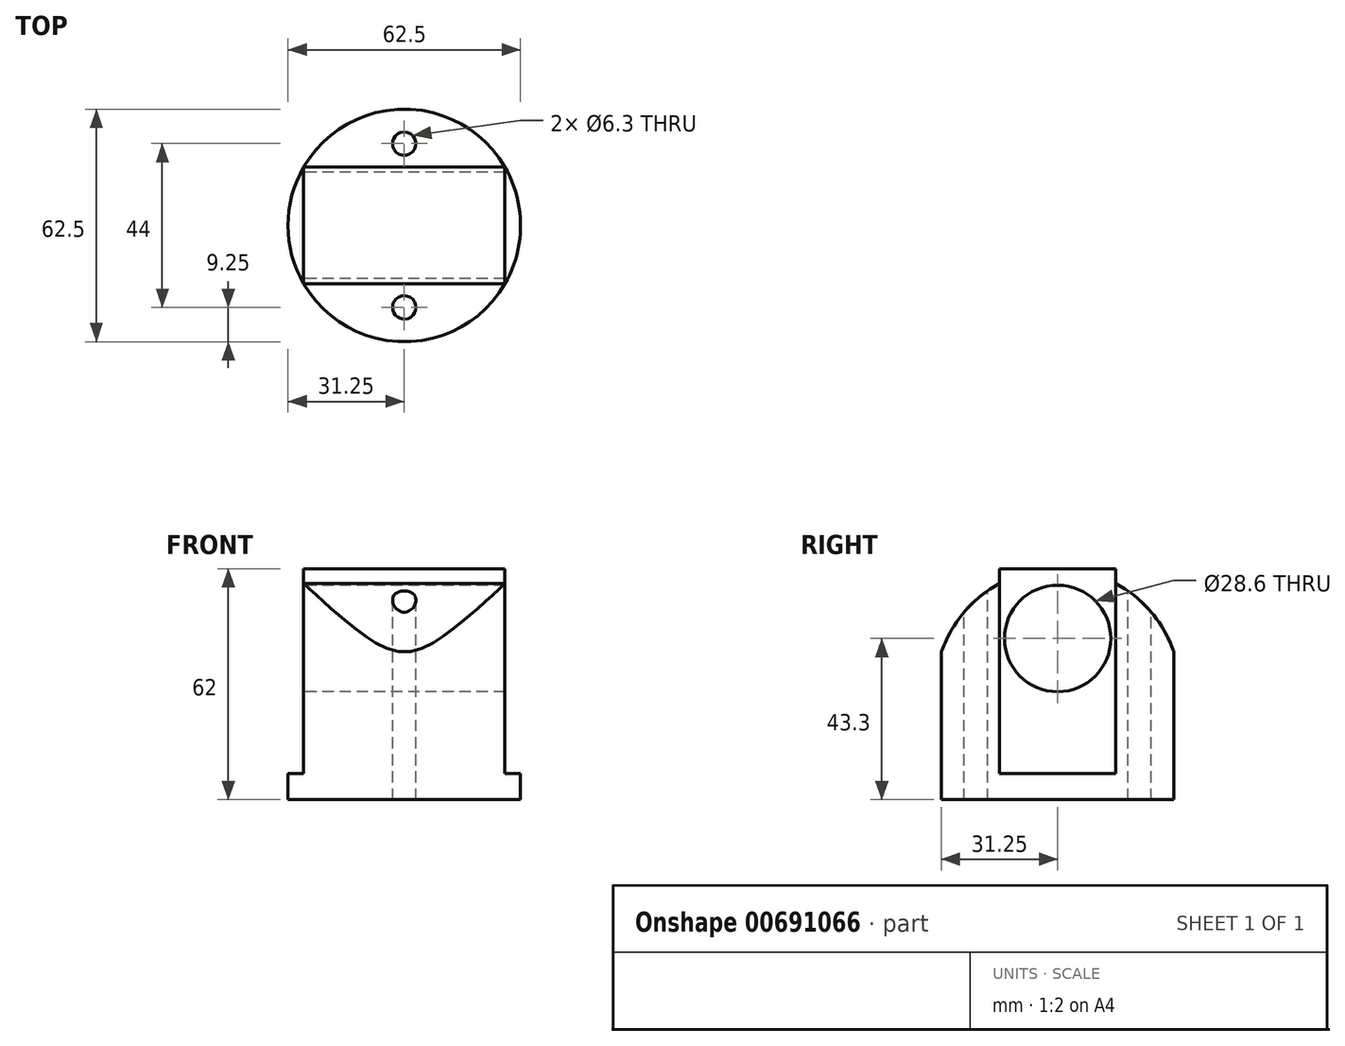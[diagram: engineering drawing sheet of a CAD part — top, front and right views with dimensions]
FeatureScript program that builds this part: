
annotation { "Feature Type Name" : "Feature", "Feature Type Description" : "" }
export const myFeature = defineFeature(function(context is Context, id is Id, definition is map)
    precondition{}
    {
        {
            var Q0;
            Q0=qCreatedBy(makeId("Top.planeOp"),FACE);
            var sketch = newSketch(context, id + "F0", { "sketchPlane" : qUnion([Q0])});
            skCircle(sketch, "E0", {"center": v(0, 0) * mm, "radius": 31.25 * mm});
            skSolve(sketch);
        }
        {
            var Q0;
            Q0=makeQuery(id+"F0.imprint","IMPRINT",FACE,{"disambiguationData":[TD([[makeQuery(id+"F0.imprint","IMPRINT",EDGE,{"derivedFrom":sQuery(id+"F0.wireOp",EDGE,"E0")}),1.0]])]});
            extrude(context, id + "F1", {"entities" : qUnion([Q0]), "depth" : 62 * mm, "offsetDistance" : 25 * mm});
        }
        {
            var Q0;
            Q0=makeQuery(id+"F1.opExtrude","CAP_FACE",FACE,{"disambiguationData":[OSD([sQuery(id+"F0.wireOp",EDGE,"E0"),sQuery(id+"F0.wireOp",EDGE,"GeYMftVd-1uso-ZqVU-DlrI-Rcq50BVMIxKk"),sQuery(id+"F0.wireOp",EDGE,"fER0mKpI-70C3-W6Zr-GIyh-661POnUvRDSi"),sQuery(id+"F0.wireOp",EDGE,"GdB3yeLU-5GCe-esW8-v4lE-ZYs1nAi0j5V2"),sQuery(id+"F0.wireOp",EDGE,"mtv5HjDL-z8JL-7D4Z-Rds9-bSP4tK6ge2Ht")])],"isStart":false});
            var sketch = newSketch(context, id + "F2", { "sketchPlane" : qUnion([Q0])});
            skLineSegment(sketch, "E1.left", {"start": v(-27.05, 15.65) * mm, "end": v(-27.05, -15.65) * mm});
            skLineSegment(sketch, "E1.right", {"start": v(27.05, 15.65) * mm, "end": v(27.05, -15.65) * mm});
            skPoint(sketch, "E1.middle", {"position": v(0, 0) * mm});
            skArc(sketch, "E2", {"start": v(-27.05, 15.65) * mm, "mid": v(-31.26, 0) * mm, "end": v(-27.05, -15.65) * mm});
            skArc(sketch, "E3", {"start": v(27.05, -15.65) * mm, "mid": v(31.25, 0) * mm, "end": v(27.05, 15.65) * mm});
            skPoint(sketch, "E1.bottom.start.orphan", {"position": v(-27.05, 28.64) * mm});
            skPoint(sketch, "E4.orphan", {"position": v(27.05, 28.64) * mm});
            skPoint(sketch, "E1.top.end.orphan", {"position": v(27.05, -28.64) * mm});
            skPoint(sketch, "E5.orphan", {"position": v(-27.05, -28.64) * mm});
            skSolve(sketch);
        }
        {
            var Q0;
            {var subQ0=sQuery(id+"F2.wireOp",EDGE,"E1.left");Q0=makeQuery(id+"F2.imprint","IMPRINT",FACE,{"disambiguationData":[TD([[makeQuery(id+"F2.imprint","IMPRINT",EDGE,{"derivedFrom":subQ0}),-1.0]])]});}
            var Q1;
            Q1=makeQuery(id+"F2.imprint","IMPRINT",FACE,{"disambiguationData":[TD([[makeQuery(id+"F2.imprint","IMPRINT",EDGE,{"derivedFrom":sQuery(id+"F2.wireOp",EDGE,"E1.right")}),1.0]])]});
            extrude(context, id + "F3", {"entities" : qUnion([Q0, Q1]), "operationType" : NewBodyOperationType.REMOVE, "oppositeDirection" : true, "depth" : 55 * mm, "offsetDistance" : 25 * mm});
        }
        {
            var Q0;
            Q0=makeQuery(id+"F3.boolean.opBoolean","COPY",FACE,{"derivedFrom":makeQuery(id+"F3.opExtrude","SWEPT_FACE",FACE,{"disambiguationData":[OSD([sQuery(id+"F2.wireOp",EDGE,"E1.left")])]})});
            var sketch = newSketch(context, id + "F4", { "sketchPlane" : qUnion([Q0])});
            skCircle(sketch, "E6", {"center": v(0, 43.3) * mm, "radius": 14.3 * mm});
            skSolve(sketch);
        }
        {
            var Q0;
            Q0=makeQuery(id+"F4.imprint","IMPRINT",FACE,{"disambiguationData":[TD([[makeQuery(id+"F4.imprint","IMPRINT",EDGE,{"derivedFrom":sQuery(id+"F4.wireOp",EDGE,"E6")}),1.0]])]});
            extrude(context, id + "F5", {"entities" : qUnion([Q0]), "operationType" : NewBodyOperationType.REMOVE, "endBound" : BoundingType.THROUGH_ALL, "oppositeDirection" : true, "depth" : 25 * mm, "offsetDistance" : 25 * mm});
        }
        {
            var Q0;
            Q0=makeQuery(id+"F1.opExtrude","CAP_FACE",FACE,{"disambiguationData":[OSD([sQuery(id+"F0.wireOp",EDGE,"E0")])],"isStart":false});
            var sketch = newSketch(context, id + "F6", { "sketchPlane" : qUnion([Q0])});
            skCircle(sketch, "E7", {"center": v(0, -22) * mm, "radius": 3.15 * mm});
            skCircle(sketch, "E8", {"center": v(0, 22) * mm, "radius": 3.15 * mm});
            skSolve(sketch);
        }
        {
            var Q0;
            Q0=makeQuery(id+"F6.imprint","IMPRINT",FACE,{"disambiguationData":[TD([[makeQuery(id+"F6.imprint","IMPRINT",EDGE,{"derivedFrom":sQuery(id+"F6.wireOp",EDGE,"E7")}),1.0]])]});
            var Q1;
            Q1=makeQuery(id+"F6.imprint","IMPRINT",FACE,{"disambiguationData":[TD([[makeQuery(id+"F6.imprint","IMPRINT",EDGE,{"derivedFrom":sQuery(id+"F6.wireOp",EDGE,"E8")}),1.0]])]});
            extrude(context, id + "F7", {"entities" : qUnion([Q0, Q1]), "operationType" : NewBodyOperationType.REMOVE, "endBound" : BoundingType.THROUGH_ALL, "oppositeDirection" : true, "depth" : 25 * mm, "offsetDistance" : 25 * mm});
        }
        {
            var Q0;
            Q0=makeQuery(id+"F3.boolean.opBoolean","COPY",FACE,{"derivedFrom":makeQuery(id+"F3.opExtrude","SWEPT_FACE",FACE,{"disambiguationData":[OSD([sQuery(id+"F2.wireOp",EDGE,"E1.right")])]})});
            var sketch = newSketch(context, id + "F8", { "sketchPlane" : qUnion([Q0])});
            skLineSegment(sketch, "E9", {"start": v(0, 62) * mm, "end": v(0, 62) * mm});
            skArc(sketch, "E10", {"start": v(33, 28.84) * mm, "mid": v(-0.47, 62) * mm, "end": v(-32.98, 27.9) * mm});
            skPoint(sketch, "E11.orphan", {"position": v(33, 0) * mm});
            skLineSegment(sketch, "E12", {"start": v(-32.98, 27.9) * mm, "end": v(-32.98, 68.42) * mm});
            skLineSegment(sketch, "E13", {"start": v(33, 28.84) * mm, "end": v(33.18, 67.77) * mm});
            skLineSegment(sketch, "E14", {"start": v(33.18, 67.77) * mm, "end": v(-32.98, 68.42) * mm});
            skSolve(sketch);
        }
        {
            var Q0;
            {var subQ0=sQuery(id+"F8.wireOp",EDGE,"E13");Q0=makeQuery(id+"F8.imprint","IMPRINT",FACE,{"disambiguationData":[TD([[makeQuery(id+"F8.imprint","IMPRINT",EDGE,{"derivedFrom":subQ0}),1.0]])]});}
            extrude(context, id + "F9", {"entities" : qUnion([Q0]), "operationType" : NewBodyOperationType.REMOVE, "endBound" : BoundingType.THROUGH_ALL, "oppositeDirection" : true, "depth" : 25 * mm, "offsetDistance" : 25 * mm});
        }
    });
